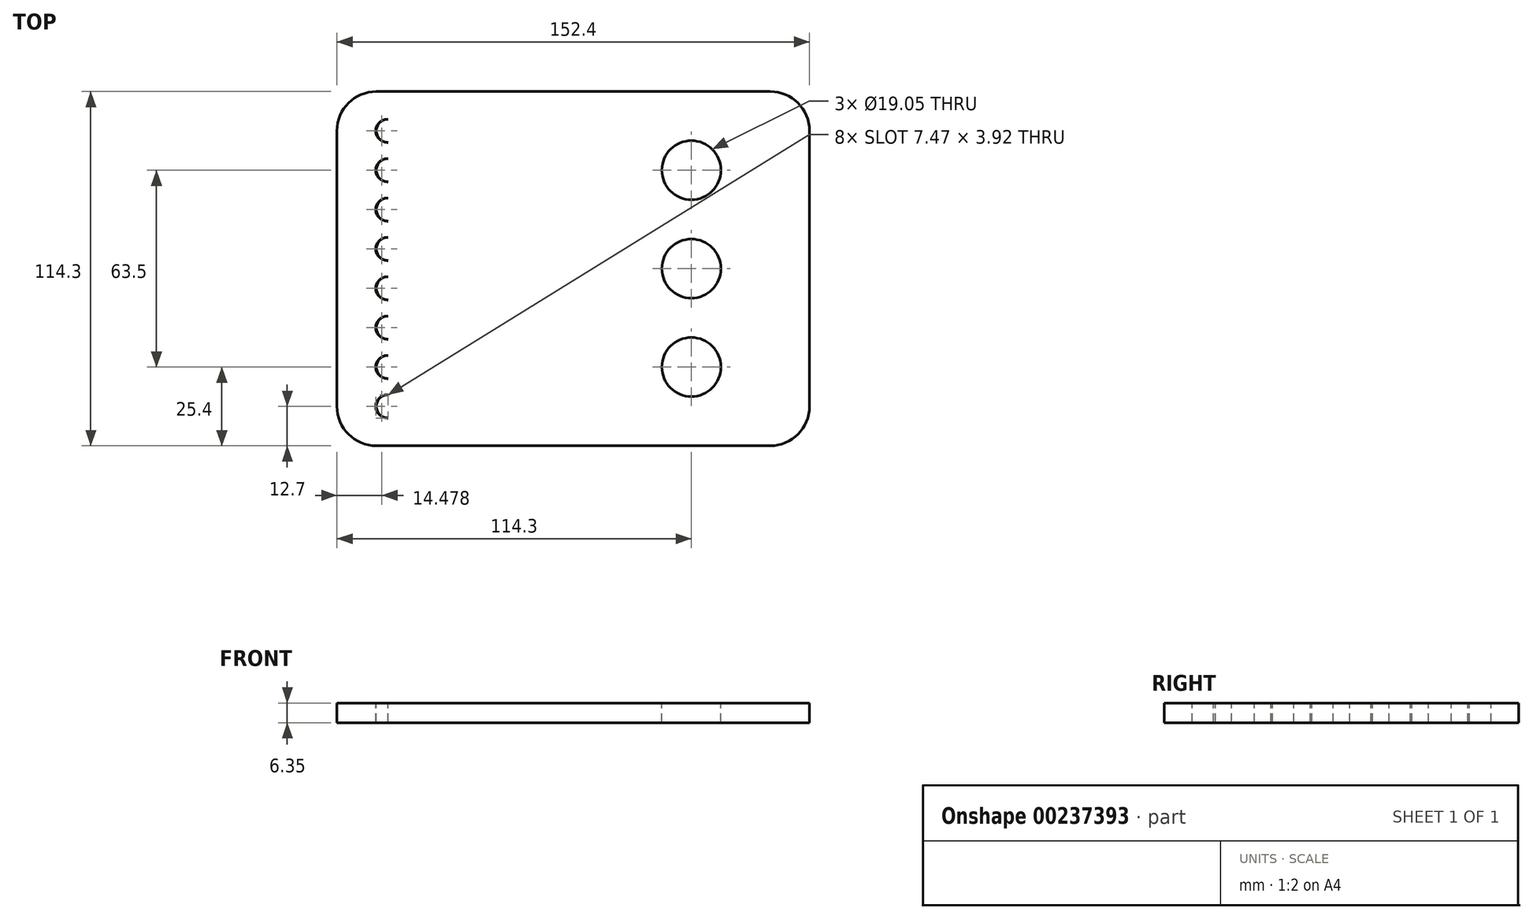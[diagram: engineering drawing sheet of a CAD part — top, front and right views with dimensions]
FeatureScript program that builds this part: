
annotation { "Feature Type Name" : "Feature", "Feature Type Description" : "" }
export const myFeature = defineFeature(function(context is Context, id is Id, definition is map)
    precondition{}
    {
        {
            var Q0;
            Q0=qCreatedBy(makeId("Top.planeOp"),FACE);
            var sketch = newSketch(context, id + "F0", { "sketchPlane" : qUnion([Q0])});
            skLineSegment(sketch, "E0.bottom", {"start": v(63.5, 57.15) * mm, "end": v(-63.5, 57.15) * mm});
            skLineSegment(sketch, "E0.top", {"start": v(63.5, -57.15) * mm, "end": v(-63.5, -57.15) * mm});
            skLineSegment(sketch, "E0.left", {"start": v(76.2, 44.45) * mm, "end": v(76.2, -44.45) * mm});
            skLineSegment(sketch, "E0.right", {"start": v(-76.2, 44.45) * mm, "end": v(-76.2, -44.45) * mm});
            skPoint(sketch, "E0.middle", {"position": v(0, 0) * mm});
            skPoint(sketch, "E1.visualSharp", {"position": v(-76.2, 57.15) * mm});
            skArc(sketch, "E1.filletArc", {"start": v(-63.5, 57.15) * mm, "mid": v(-72.48, 53.43) * mm, "end": v(-76.2, 44.45) * mm});
            skPoint(sketch, "E2.visualSharp", {"position": v(-76.2, -57.15) * mm});
            skArc(sketch, "E2.filletArc", {"start": v(-76.2, -44.45) * mm, "mid": v(-72.48, -53.43) * mm, "end": v(-63.5, -57.15) * mm});
            skPoint(sketch, "E3.visualSharp", {"position": v(76.2, -57.15) * mm});
            skArc(sketch, "E3.filletArc", {"start": v(63.5, -57.15) * mm, "mid": v(72.48, -53.43) * mm, "end": v(76.2, -44.45) * mm});
            skPoint(sketch, "E4.visualSharp", {"position": v(76.2, 57.15) * mm});
            skArc(sketch, "E4.filletArc", {"start": v(76.2, 44.45) * mm, "mid": v(72.48, 53.43) * mm, "end": v(63.5, 57.15) * mm});
            skSolve(sketch);
        }
        {
            var Q0;
            Q0=makeQuery(id+"F0.imprint","IMPRINT",FACE,{"disambiguationData":[TD([[makeQuery(id+"F0.imprint","IMPRINT",EDGE,{"derivedFrom":sQuery(id+"F0.wireOp",EDGE,"E0.bottom")}),1.0]])]});
            extrude(context, id + "F1", {"entities" : qUnion([Q0]), "depth" : 6.35 * mm});
        }
        {
            var Q0;
            Q0=makeQuery(id+"F1.opExtrude","CAP_FACE",FACE,{"disambiguationData":[OSD([sQuery(id+"F0.wireOp",EDGE,"E0.bottom"),sQuery(id+"F0.wireOp",EDGE,"E0.top"),sQuery(id+"F0.wireOp",EDGE,"E0.left"),sQuery(id+"F0.wireOp",EDGE,"E0.right"),sQuery(id+"F0.wireOp",EDGE,"E1.filletArc"),sQuery(id+"F0.wireOp",EDGE,"E2.filletArc"),sQuery(id+"F0.wireOp",EDGE,"E3.filletArc"),sQuery(id+"F0.wireOp",EDGE,"E4.filletArc")])],"isStart":false});
            var sketch = newSketch(context, id + "F2", { "sketchPlane" : qUnion([Q0])});
            skCircle(sketch, "E5", {"center": v(38.1, 31.75) * mm, "radius": 9.53 * mm});
            skCircle(sketch, "E6", {"center": v(38.1, 0) * mm, "radius": 9.53 * mm});
            skCircle(sketch, "E7", {"center": v(38.1, -31.75) * mm, "radius": 9.53 * mm});
            skSolve(sketch);
        }
        {
            var Q0;
            Q0 = qSketchRegion(id + "F2", true);
            extrude(context, id + "F3", {"entities" : qUnion([Q0]), "operationType" : NewBodyOperationType.REMOVE, "endBound" : BoundingType.THROUGH_ALL, "oppositeDirection" : true, "depth" : 25.4 * mm});
        }
        {
            var Q0;
            Q0=makeQuery(id+"F1.opExtrude","CAP_FACE",FACE,{"disambiguationData":[OSD([sQuery(id+"F0.wireOp",EDGE,"E0.bottom"),sQuery(id+"F0.wireOp",EDGE,"E0.top"),sQuery(id+"F0.wireOp",EDGE,"E0.left"),sQuery(id+"F0.wireOp",EDGE,"E0.right"),sQuery(id+"F0.wireOp",EDGE,"E1.filletArc"),sQuery(id+"F0.wireOp",EDGE,"E2.filletArc"),sQuery(id+"F0.wireOp",EDGE,"E3.filletArc"),sQuery(id+"F0.wireOp",EDGE,"E4.filletArc")])],"isStart":false});
            var sketch = newSketch(context, id + "F4", { "sketchPlane" : qUnion([Q0])});
            skLineSegment(sketch, "E8.bottom", {"start": v(-8.96, -48.19) * mm, "end": v(-59.76, -48.19) * mm});
            skLineSegment(sketch, "E8.top", {"start": v(-8.96, -40.71) * mm, "end": v(-59.76, -40.71) * mm});
            skPoint(sketch, "E8.middle", {"position": v(-34.36, -44.45) * mm});
            skArc(sketch, "E9", {"start": v(-8.96, -40.71) * mm, "mid": v(-5.23, -44.45) * mm, "end": v(-8.96, -48.19) * mm});
            skArc(sketch, "E10", {"start": v(-59.76, -48.19) * mm, "mid": v(-63.5, -44.45) * mm, "end": v(-59.76, -40.71) * mm});
            skArc(sketch, "E11.0.1.0", {"start": v(-59.76, -35.49) * mm, "mid": v(-63.5, -31.75) * mm, "end": v(-59.76, -28.01) * mm});
            skLineSegment(sketch, "E11.0.1.1", {"start": v(-8.96, -35.49) * mm, "end": v(-59.76, -35.49) * mm});
            skArc(sketch, "E11.0.1.2", {"start": v(-8.96, -28.01) * mm, "mid": v(-5.23, -31.75) * mm, "end": v(-8.96, -35.49) * mm});
            skLineSegment(sketch, "E11.0.1.3", {"start": v(-8.96, -28.01) * mm, "end": v(-59.76, -28.01) * mm});
            skArc(sketch, "E11.0.2.0", {"start": v(-59.76, -22.79) * mm, "mid": v(-63.5, -19.05) * mm, "end": v(-59.76, -15.31) * mm});
            skLineSegment(sketch, "E11.0.2.1", {"start": v(-8.96, -22.79) * mm, "end": v(-59.76, -22.79) * mm});
            skArc(sketch, "E11.0.2.2", {"start": v(-8.96, -15.31) * mm, "mid": v(-5.23, -19.05) * mm, "end": v(-8.96, -22.79) * mm});
            skLineSegment(sketch, "E11.0.2.3", {"start": v(-8.96, -15.31) * mm, "end": v(-59.76, -15.31) * mm});
            skArc(sketch, "E11.0.3.0", {"start": v(-59.76, -10.09) * mm, "mid": v(-63.5, -6.35) * mm, "end": v(-59.76, -2.61) * mm});
            skLineSegment(sketch, "E11.0.3.1", {"start": v(-8.96, -10.09) * mm, "end": v(-59.76, -10.09) * mm});
            skArc(sketch, "E11.0.3.2", {"start": v(-8.96, -2.61) * mm, "mid": v(-5.23, -6.35) * mm, "end": v(-8.96, -10.09) * mm});
            skLineSegment(sketch, "E11.0.3.3", {"start": v(-8.96, -2.61) * mm, "end": v(-59.76, -2.61) * mm});
            skArc(sketch, "E11.0.4.0", {"start": v(-59.76, 2.61) * mm, "mid": v(-63.5, 6.35) * mm, "end": v(-59.76, 10.09) * mm});
            skLineSegment(sketch, "E11.0.4.1", {"start": v(-8.96, 2.61) * mm, "end": v(-59.76, 2.61) * mm});
            skArc(sketch, "E11.0.4.2", {"start": v(-8.96, 10.09) * mm, "mid": v(-5.23, 6.35) * mm, "end": v(-8.96, 2.61) * mm});
            skLineSegment(sketch, "E11.0.4.3", {"start": v(-8.96, 10.09) * mm, "end": v(-59.76, 10.09) * mm});
            skArc(sketch, "E11.0.5.0", {"start": v(-59.76, 15.31) * mm, "mid": v(-63.5, 19.05) * mm, "end": v(-59.76, 22.79) * mm});
            skLineSegment(sketch, "E11.0.5.1", {"start": v(-8.96, 15.31) * mm, "end": v(-59.76, 15.31) * mm});
            skArc(sketch, "E11.0.5.2", {"start": v(-8.96, 22.79) * mm, "mid": v(-5.23, 19.05) * mm, "end": v(-8.96, 15.31) * mm});
            skLineSegment(sketch, "E11.0.5.3", {"start": v(-8.96, 22.79) * mm, "end": v(-59.76, 22.79) * mm});
            skArc(sketch, "E11.0.6.0", {"start": v(-59.76, 28.01) * mm, "mid": v(-63.5, 31.75) * mm, "end": v(-59.76, 35.49) * mm});
            skLineSegment(sketch, "E11.0.6.1", {"start": v(-8.96, 28.01) * mm, "end": v(-59.76, 28.01) * mm});
            skArc(sketch, "E11.0.6.2", {"start": v(-8.96, 35.49) * mm, "mid": v(-5.23, 31.75) * mm, "end": v(-8.96, 28.01) * mm});
            skLineSegment(sketch, "E11.0.6.3", {"start": v(-8.96, 35.49) * mm, "end": v(-59.76, 35.49) * mm});
            skArc(sketch, "E11.0.7.0", {"start": v(-59.76, 40.71) * mm, "mid": v(-63.5, 44.45) * mm, "end": v(-59.76, 48.19) * mm});
            skLineSegment(sketch, "E11.0.7.1", {"start": v(-8.96, 40.71) * mm, "end": v(-59.76, 40.71) * mm});
            skArc(sketch, "E11.0.7.2", {"start": v(-8.96, 48.19) * mm, "mid": v(-5.23, 44.45) * mm, "end": v(-8.96, 40.71) * mm});
            skLineSegment(sketch, "E11.0.7.3", {"start": v(-8.96, 48.19) * mm, "end": v(-59.76, 48.19) * mm});
            skArc(sketch, "E11.1.0.0", {"start": v(-59.94, -48.19) * mm, "mid": v(-63.68, -44.45) * mm, "end": v(-59.94, -40.71) * mm});
            skLineSegment(sketch, "E11.1.0.1", {"start": v(-9.14, -48.19) * mm, "end": v(-59.94, -48.19) * mm});
            skArc(sketch, "E11.1.0.2", {"start": v(-9.14, -40.71) * mm, "mid": v(-5.4, -44.45) * mm, "end": v(-9.14, -48.19) * mm});
            skLineSegment(sketch, "E11.1.0.3", {"start": v(-9.14, -40.71) * mm, "end": v(-59.94, -40.71) * mm});
            skArc(sketch, "E11.1.1.0", {"start": v(-59.94, -35.49) * mm, "mid": v(-63.68, -31.75) * mm, "end": v(-59.94, -28.01) * mm});
            skLineSegment(sketch, "E11.1.1.1", {"start": v(-9.14, -35.49) * mm, "end": v(-59.94, -35.49) * mm});
            skArc(sketch, "E11.1.1.2", {"start": v(-9.14, -28.01) * mm, "mid": v(-5.4, -31.75) * mm, "end": v(-9.14, -35.49) * mm});
            skLineSegment(sketch, "E11.1.1.3", {"start": v(-9.14, -28.01) * mm, "end": v(-59.94, -28.01) * mm});
            skArc(sketch, "E11.1.2.0", {"start": v(-59.94, -22.79) * mm, "mid": v(-63.68, -19.05) * mm, "end": v(-59.94, -15.31) * mm});
            skLineSegment(sketch, "E11.1.2.1", {"start": v(-9.14, -22.79) * mm, "end": v(-59.94, -22.79) * mm});
            skArc(sketch, "E11.1.2.2", {"start": v(-9.14, -15.31) * mm, "mid": v(-5.4, -19.05) * mm, "end": v(-9.14, -22.79) * mm});
            skLineSegment(sketch, "E11.1.2.3", {"start": v(-9.14, -15.31) * mm, "end": v(-59.94, -15.31) * mm});
            skArc(sketch, "E11.1.3.0", {"start": v(-59.94, -10.09) * mm, "mid": v(-63.68, -6.35) * mm, "end": v(-59.94, -2.61) * mm});
            skLineSegment(sketch, "E11.1.3.1", {"start": v(-9.14, -10.09) * mm, "end": v(-59.94, -10.09) * mm});
            skArc(sketch, "E11.1.3.2", {"start": v(-9.14, -2.61) * mm, "mid": v(-5.4, -6.35) * mm, "end": v(-9.14, -10.09) * mm});
            skLineSegment(sketch, "E11.1.3.3", {"start": v(-9.14, -2.61) * mm, "end": v(-59.94, -2.61) * mm});
            skArc(sketch, "E11.1.4.0", {"start": v(-59.94, 2.61) * mm, "mid": v(-63.68, 6.35) * mm, "end": v(-59.94, 10.09) * mm});
            skLineSegment(sketch, "E11.1.4.1", {"start": v(-9.14, 2.61) * mm, "end": v(-59.94, 2.61) * mm});
            skArc(sketch, "E11.1.4.2", {"start": v(-9.14, 10.09) * mm, "mid": v(-5.4, 6.35) * mm, "end": v(-9.14, 2.61) * mm});
            skLineSegment(sketch, "E11.1.4.3", {"start": v(-9.14, 10.09) * mm, "end": v(-59.94, 10.09) * mm});
            skArc(sketch, "E11.1.5.0", {"start": v(-59.94, 15.31) * mm, "mid": v(-63.68, 19.05) * mm, "end": v(-59.94, 22.79) * mm});
            skLineSegment(sketch, "E11.1.5.1", {"start": v(-9.14, 15.31) * mm, "end": v(-59.94, 15.31) * mm});
            skArc(sketch, "E11.1.5.2", {"start": v(-9.14, 22.79) * mm, "mid": v(-5.4, 19.05) * mm, "end": v(-9.14, 15.31) * mm});
            skLineSegment(sketch, "E11.1.5.3", {"start": v(-9.14, 22.79) * mm, "end": v(-59.94, 22.79) * mm});
            skArc(sketch, "E11.1.6.0", {"start": v(-59.94, 28.01) * mm, "mid": v(-63.68, 31.75) * mm, "end": v(-59.94, 35.49) * mm});
            skLineSegment(sketch, "E11.1.6.1", {"start": v(-9.14, 28.01) * mm, "end": v(-59.94, 28.01) * mm});
            skArc(sketch, "E11.1.6.2", {"start": v(-9.14, 35.49) * mm, "mid": v(-5.4, 31.75) * mm, "end": v(-9.14, 28.01) * mm});
            skLineSegment(sketch, "E11.1.6.3", {"start": v(-9.14, 35.49) * mm, "end": v(-59.94, 35.49) * mm});
            skArc(sketch, "E11.1.7.0", {"start": v(-59.94, 40.71) * mm, "mid": v(-63.68, 44.45) * mm, "end": v(-59.94, 48.19) * mm});
            skLineSegment(sketch, "E11.1.7.1", {"start": v(-9.14, 40.71) * mm, "end": v(-59.94, 40.71) * mm});
            skArc(sketch, "E11.1.7.2", {"start": v(-9.14, 48.19) * mm, "mid": v(-5.4, 44.45) * mm, "end": v(-9.14, 40.71) * mm});
            skLineSegment(sketch, "E11.1.7.3", {"start": v(-9.14, 48.19) * mm, "end": v(-59.94, 48.19) * mm});
            skArc(sketch, "E11.2.0.0", {"start": v(-60.12, -48.19) * mm, "mid": v(-63.86, -44.45) * mm, "end": v(-60.12, -40.71) * mm});
            skLineSegment(sketch, "E11.2.0.1", {"start": v(-9.32, -48.19) * mm, "end": v(-60.12, -48.19) * mm});
            skArc(sketch, "E11.2.0.2", {"start": v(-9.32, -40.71) * mm, "mid": v(-5.59, -44.45) * mm, "end": v(-9.32, -48.19) * mm});
            skLineSegment(sketch, "E11.2.0.3", {"start": v(-9.32, -40.71) * mm, "end": v(-60.12, -40.71) * mm});
            skArc(sketch, "E11.2.1.0", {"start": v(-60.12, -35.49) * mm, "mid": v(-63.86, -31.75) * mm, "end": v(-60.12, -28.01) * mm});
            skLineSegment(sketch, "E11.2.1.1", {"start": v(-9.32, -35.49) * mm, "end": v(-60.12, -35.49) * mm});
            skArc(sketch, "E11.2.1.2", {"start": v(-9.32, -28.01) * mm, "mid": v(-5.59, -31.75) * mm, "end": v(-9.32, -35.49) * mm});
            skLineSegment(sketch, "E11.2.1.3", {"start": v(-9.32, -28.01) * mm, "end": v(-60.12, -28.01) * mm});
            skArc(sketch, "E11.2.2.0", {"start": v(-60.12, -22.79) * mm, "mid": v(-63.86, -19.05) * mm, "end": v(-60.12, -15.31) * mm});
            skLineSegment(sketch, "E11.2.2.1", {"start": v(-9.32, -22.79) * mm, "end": v(-60.12, -22.79) * mm});
            skArc(sketch, "E11.2.2.2", {"start": v(-9.32, -15.31) * mm, "mid": v(-5.59, -19.05) * mm, "end": v(-9.32, -22.79) * mm});
            skLineSegment(sketch, "E11.2.2.3", {"start": v(-9.32, -15.31) * mm, "end": v(-60.12, -15.31) * mm});
            skArc(sketch, "E11.2.3.0", {"start": v(-60.12, -10.09) * mm, "mid": v(-63.86, -6.35) * mm, "end": v(-60.12, -2.61) * mm});
            skLineSegment(sketch, "E11.2.3.1", {"start": v(-9.32, -10.09) * mm, "end": v(-60.12, -10.09) * mm});
            skArc(sketch, "E11.2.3.2", {"start": v(-9.32, -2.61) * mm, "mid": v(-5.59, -6.35) * mm, "end": v(-9.32, -10.09) * mm});
            skLineSegment(sketch, "E11.2.3.3", {"start": v(-9.32, -2.61) * mm, "end": v(-60.12, -2.61) * mm});
            skArc(sketch, "E11.2.4.0", {"start": v(-60.12, 2.61) * mm, "mid": v(-63.86, 6.35) * mm, "end": v(-60.12, 10.09) * mm});
            skLineSegment(sketch, "E11.2.4.1", {"start": v(-9.32, 2.61) * mm, "end": v(-60.12, 2.61) * mm});
            skArc(sketch, "E11.2.4.2", {"start": v(-9.32, 10.09) * mm, "mid": v(-5.59, 6.35) * mm, "end": v(-9.32, 2.61) * mm});
            skLineSegment(sketch, "E11.2.4.3", {"start": v(-9.32, 10.09) * mm, "end": v(-60.12, 10.09) * mm});
            skArc(sketch, "E11.2.5.0", {"start": v(-60.12, 15.31) * mm, "mid": v(-63.86, 19.05) * mm, "end": v(-60.12, 22.79) * mm});
            skLineSegment(sketch, "E11.2.5.1", {"start": v(-9.32, 15.31) * mm, "end": v(-60.12, 15.31) * mm});
            skArc(sketch, "E11.2.5.2", {"start": v(-9.32, 22.79) * mm, "mid": v(-5.59, 19.05) * mm, "end": v(-9.32, 15.31) * mm});
            skLineSegment(sketch, "E11.2.5.3", {"start": v(-9.32, 22.79) * mm, "end": v(-60.12, 22.79) * mm});
            skArc(sketch, "E11.2.6.0", {"start": v(-60.12, 28.01) * mm, "mid": v(-63.86, 31.75) * mm, "end": v(-60.12, 35.49) * mm});
            skLineSegment(sketch, "E11.2.6.1", {"start": v(-9.32, 28.01) * mm, "end": v(-60.12, 28.01) * mm});
            skArc(sketch, "E11.2.6.2", {"start": v(-9.32, 35.49) * mm, "mid": v(-5.59, 31.75) * mm, "end": v(-9.32, 28.01) * mm});
            skLineSegment(sketch, "E11.2.6.3", {"start": v(-9.32, 35.49) * mm, "end": v(-60.12, 35.49) * mm});
            skArc(sketch, "E11.2.7.0", {"start": v(-60.12, 40.71) * mm, "mid": v(-63.86, 44.45) * mm, "end": v(-60.12, 48.19) * mm});
            skLineSegment(sketch, "E11.2.7.1", {"start": v(-9.32, 40.71) * mm, "end": v(-60.12, 40.71) * mm});
            skArc(sketch, "E11.2.7.2", {"start": v(-9.32, 48.19) * mm, "mid": v(-5.59, 44.45) * mm, "end": v(-9.32, 40.71) * mm});
            skLineSegment(sketch, "E11.2.7.3", {"start": v(-9.32, 48.19) * mm, "end": v(-60.12, 48.19) * mm});
            skLineSegment(sketch, "E11.direction1", {"start": v(-59.76, -48.19) * mm, "end": v(-59.94, -48.19) * mm, "construction": true});
            skLineSegment(sketch, "E11.direction2", {"start": v(-59.76, -48.19) * mm, "end": v(-59.76, -35.49) * mm, "construction": true});
            skSolve(sketch);
        }
        {
            var Q0;
            {var subQ0=sQuery(id+"F4.wireOp",EDGE,"E10");Q0=makeQuery(id+"F4.imprint","IMPRINT",FACE,{"disambiguationData":[TD([[makeQuery(id+"F4.imprint","IMPRINT",EDGE,{"derivedFrom":subQ0}),-1.0]])]});}
            var Q1;
            {var subQ0=sQuery(id+"F4.wireOp",EDGE,"E11.0.1.0");Q1=makeQuery(id+"F4.imprint","IMPRINT",FACE,{"disambiguationData":[TD([[makeQuery(id+"F4.imprint","IMPRINT",EDGE,{"derivedFrom":subQ0}),-1.0]])]});}
            var Q2;
            {var subQ0=sQuery(id+"F4.wireOp",EDGE,"E11.0.2.0");Q2=makeQuery(id+"F4.imprint","IMPRINT",FACE,{"disambiguationData":[TD([[makeQuery(id+"F4.imprint","IMPRINT",EDGE,{"derivedFrom":subQ0}),-1.0]])]});}
            var Q3;
            {var subQ0=sQuery(id+"F4.wireOp",EDGE,"E11.0.3.0");Q3=makeQuery(id+"F4.imprint","IMPRINT",FACE,{"disambiguationData":[TD([[makeQuery(id+"F4.imprint","IMPRINT",EDGE,{"derivedFrom":subQ0}),-1.0]])]});}
            var Q4;
            {var subQ0=sQuery(id+"F4.wireOp",EDGE,"E11.0.4.0");Q4=makeQuery(id+"F4.imprint","IMPRINT",FACE,{"disambiguationData":[TD([[makeQuery(id+"F4.imprint","IMPRINT",EDGE,{"derivedFrom":subQ0}),-1.0]])]});}
            var Q5;
            {var subQ0=sQuery(id+"F4.wireOp",EDGE,"E11.0.5.0");Q5=makeQuery(id+"F4.imprint","IMPRINT",FACE,{"disambiguationData":[TD([[makeQuery(id+"F4.imprint","IMPRINT",EDGE,{"derivedFrom":subQ0}),-1.0]])]});}
            var Q6;
            {var subQ0=sQuery(id+"F4.wireOp",EDGE,"E11.0.6.0");Q6=makeQuery(id+"F4.imprint","IMPRINT",FACE,{"disambiguationData":[TD([[makeQuery(id+"F4.imprint","IMPRINT",EDGE,{"derivedFrom":subQ0}),-1.0]])]});}
            var Q7;
            {var subQ0=sQuery(id+"F4.wireOp",EDGE,"E11.0.7.0");Q7=makeQuery(id+"F4.imprint","IMPRINT",FACE,{"disambiguationData":[TD([[makeQuery(id+"F4.imprint","IMPRINT",EDGE,{"derivedFrom":subQ0}),-1.0]])]});}
            extrude(context, id + "F5", {"entities" : qUnion([Q0, Q1, Q2, Q3, Q4, Q5, Q6, Q7]), "operationType" : NewBodyOperationType.REMOVE, "endBound" : BoundingType.THROUGH_ALL, "oppositeDirection" : true, "depth" : 25.4 * mm});
        }
    });
